# Revit family: IS_IdealSystem_W3710_BIM_NL
name_source: partatom
category: Plumbing Fixtures
revit_build: Autodesk Revit MEP 2014 (Build: 20140709_2115(x64)
units: mm (PartAtom-declared; Revit-internal decimal feet)

## types (1)
- W3710AA - INBOUWRESERVOIR MET AFDEKPLAAT CHROOM IS
    Accessories = www.idealstandardnederland.nl
    AreaUnits = millimeters
    Assembly Code = C1030200
    AssetType = Vast
    BREEAMApproved = No
    BarCode = 3800828021815
    Brand = Ideal Standard
    CWFU = 0
    ConnectionType = Sanitair
    Cost = 0 $
    Default Elevation = 0 mm  [stored 0 ft]
    Description = Inbouwspoelreservoir inclusief drukplaat verchroomd. 3/6 liter spoeling.
    DurationUnit = jaar
    ECA = No
    ExpectedLife = 25
    Features = Inbouwspoelreservoir inclusief drukplaat verchroomd. 3/6 liter spoeling.
    Finish = Chroom
    HWFU = 0
    IfcExportAs = IfcSanitaryTerminalType
    IfcExportType = Inbouwspoelreservoir
    InstallationInstructions = http://www.idealstandardnederland.nl
    LinearUnits = millimeters
    ManufacturerURL = www.idealstandardnederland.nl
    Model = W3710AA
    ModelNumber = W3710AA
    ModelReference = Inbouwspoelreservoir inclusief drukplaat verchroomd. 3/6 liter spoeling.
    NBSDescription = WC cistern fittings
    NBSReference = 45-30-70/387
    Name = INBOUWRESERVOIR MET AFDEKPLAAT CHROOM IS
    NettWeight = 11 Kg
    NominalDepth = 333 mm
    NominalLength = 0 mm  [stored 0 ft]
    NominalWidth = 350 mm  [stored 1.14829 ft]
    ProductInformation = http://www.idealstandardnederland.nl
    Shape = Sculptured
    Size = 350 x 262 x 1100 mm
    Space = Internal
    SpilloverLevel = 0 mm  [stored 0 ft]
    URL = www.idealstandardnederland.nl
    Uniclass2 = Pr_40_20_93_89
    Version = 1
    VolumeUnits = liter
    WFU = 0
    WRAS = No
    WarrantyDescription = Fabrieksgarantie
    WarrantyDurationParts = 5
    WarrantyDurationUnit = jaar
    WaterEfficientProduct = No

note: [stored X ft] marks values corroborated as IEEE doubles in the binary element streams (Revit-internal decimal feet)

## geometry (parser evidence)
native form markers: Sweep x9
no freeform markers — native parametric forms only
